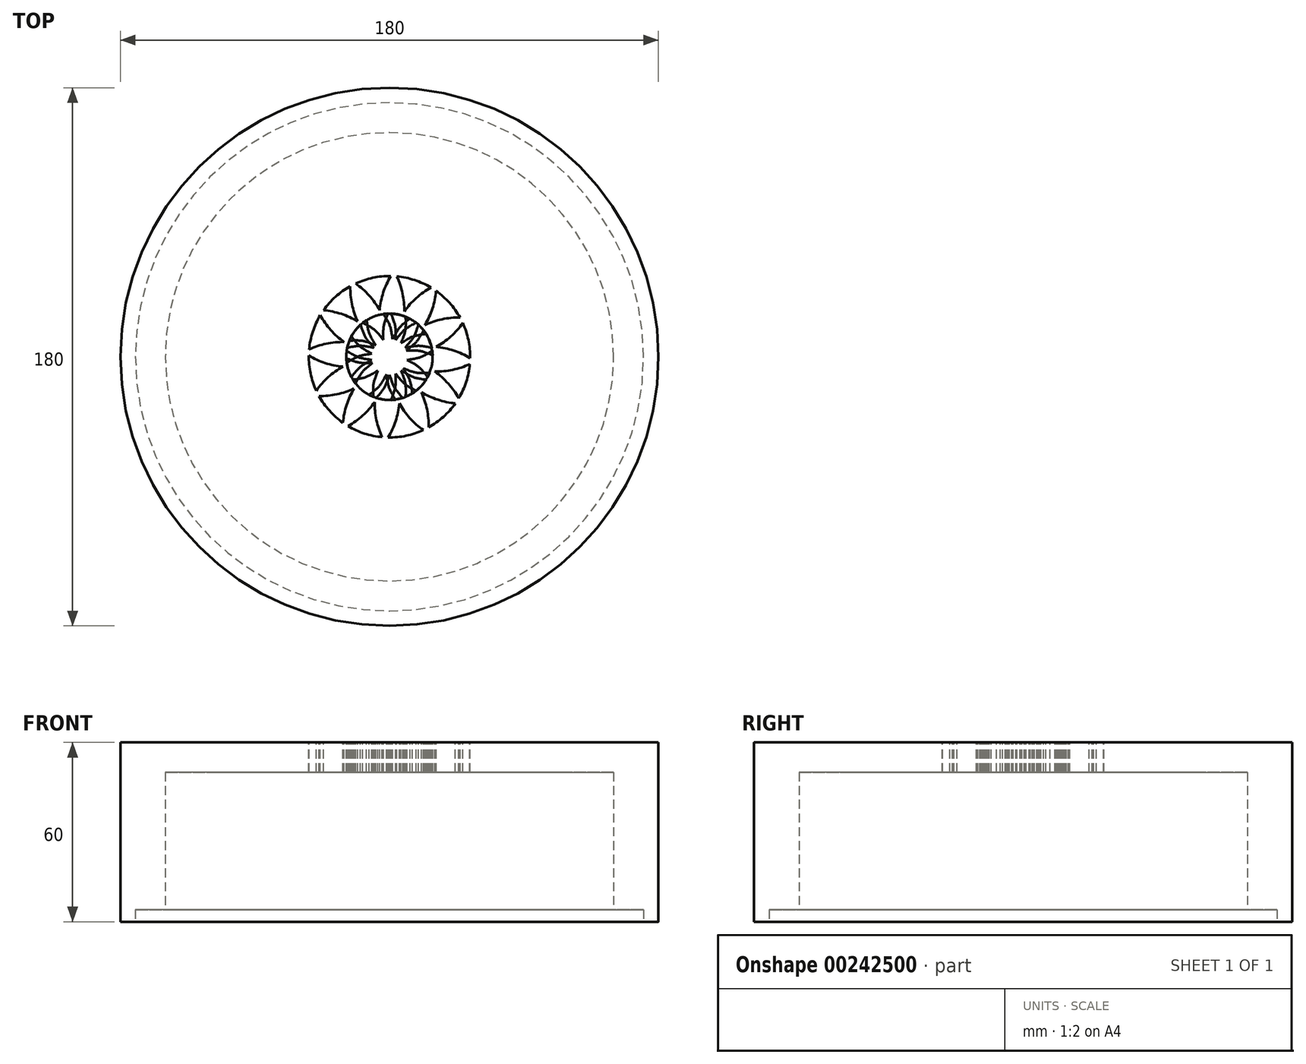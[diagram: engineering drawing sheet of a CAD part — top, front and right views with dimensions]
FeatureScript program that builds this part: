
annotation { "Feature Type Name" : "Feature", "Feature Type Description" : "" }
export const myFeature = defineFeature(function(context is Context, id is Id, definition is map)
    precondition{}
    {
        {
            var Q0;
            Q0=qCreatedBy(makeId("Top.planeOp"),FACE);
            var sketch = newSketch(context, id + "F0", { "sketchPlane" : qUnion([Q0])});
            skLineSegment(sketch, "E0", {"start": v(0, 117.16) * mm, "end": v(0, -101.17) * mm, "construction": true});
            skLineSegment(sketch, "E1", {"start": v(-126.7, 0) * mm, "end": v(131.73, 0) * mm, "construction": true});
            skLineSegment(sketch, "E2", {"start": v(0, -6) * mm, "end": v(-4.5, -13.8) * mm, "construction": true});
            skLineSegment(sketch, "E3", {"start": v(-4.5, -13.8) * mm, "end": v(4.5, -13.8) * mm, "construction": true});
            skLineSegment(sketch, "E4", {"start": v(4.5, -13.8) * mm, "end": v(0, -6) * mm, "construction": true});
            skLineSegment(sketch, "E5", {"start": v(0, -6) * mm, "end": v(0, -13.8) * mm, "construction": true});
            skFitSpline(sketch, "E6", {"points": [v(-4.5, -13.8) * mm, v(4.5, -13.8) * mm], "startDerivative": vector(13.5, -2.7) * mm, "endDerivative": vector(13.5, 2.7) * mm});
            skFitSpline(sketch, "E7", {"points": [v(-4.5, -13.8) * mm, v(0, -6) * mm], "startDerivative": vector(9.09, 10.34) * mm, "endDerivative": vector(4.41, 13.04) * mm});
            skLineSegment(sketch, "E8", {"start": v(4.5, -13.8) * mm, "end": v(-1.47, -10.35) * mm, "construction": true});
            skLineSegment(sketch, "E9", {"start": v(-4.5, -13.8) * mm, "end": v(1.47, -10.35) * mm, "construction": true});
            skFitSpline(sketch, "E10", {"points": [v(0, -6) * mm, v(4.5, -13.8) * mm], "startDerivative": vector(4.41, -13.04) * mm, "endDerivative": vector(9.09, -10.34) * mm});
            skSolve(sketch);
        }
        {
            var Q0;
            Q0=qCreatedBy(makeId("Top.planeOp"),FACE);
            var sketch = newSketch(context, id + "F1", { "sketchPlane" : qUnion([Q0])});
            skCircle(sketch, "E11", {"center": v(0, 0) * mm, "radius": 90 * mm});
            skSolve(sketch);
        }
        {
            var Q0;
            Q0 = qSketchRegion(id + "F1", true);
            extrude(context, id + "F2", {"entities" : qUnion([Q0]), "oppositeDirection" : true, "depth" : 60 * mm});
        }
        {
            var Q0;
            Q0=makeQuery(id+"F2.opExtrude","CAP_FACE",FACE,{"disambiguationData":[OSD([sQuery(id+"F1.wireOp",EDGE,"E11")])],"isStart":false});
            var sketch = newSketch(context, id + "F3", { "sketchPlane" : qUnion([Q0])});
            skCircle(sketch, "E12", {"center": v(0, 0) * mm, "radius": 85 * mm});
            skCircle(sketch, "E13", {"center": v(0, 0) * mm, "radius": 75 * mm});
            skSolve(sketch);
        }
        {
            var Q0;
            Q0 = qSketchRegion(id + "F3", true);
            extrude(context, id + "F4", {"entities" : qUnion([Q0]), "operationType" : NewBodyOperationType.REMOVE, "oppositeDirection" : true, "depth" : 4 * mm});
        }
        {
            var Q0;
            Q0=makeQuery(id+"F4.boolean.opBoolean","SPLIT",FACE,{"disambiguationData":[TD([makeQuery(id+"F4.opExtrude","SWEPT_FACE",FACE,{"disambiguationData":[OSD([sQuery(id+"F3.wireOp",EDGE,"E13")])]})])],"derivedFrom":makeQuery(id+"F2.opExtrude","CAP_FACE",FACE,{"disambiguationData":[OSD([sQuery(id+"F1.wireOp",EDGE,"E11")])],"isStart":false})});
            var sketch = newSketch(context, id + "F5", { "sketchPlane" : qUnion([Q0])});
            skSolve(sketch);
        }
        {
            var Q0;
            Q0=makeQuery(id+"F5.imprint","IMPRINT",FACE,{"disambiguationData":[TD([[makeQuery(id+"F5.imprint","IMPRINT",EDGE,{"derivedFrom":makeQuery(id+"F4.boolean.opBoolean","COPY",EDGE,{"derivedFrom":makeQuery(id+"F4.opExtrude","CAP_EDGE",EDGE,{"disambiguationData":[OSD([sQuery(id+"F3.wireOp",EDGE,"E13")])],"isStart":true})})}),1.0]])]});
            var sketch = newSketch(context, id + "F6", { "sketchPlane" : qUnion([Q0])});
            skCircle(sketch, "E14", {"center": v(0, 0) * mm, "radius": 75 * mm});
            skSolve(sketch);
        }
        {
            var Q0;
            Q0=makeQuery(id+"F5.imprint","IMPRINT",FACE,{"disambiguationData":[TD([[makeQuery(id+"F5.imprint","IMPRINT",EDGE,{"derivedFrom":makeQuery(id+"F4.boolean.opBoolean","COPY",EDGE,{"derivedFrom":makeQuery(id+"F4.opExtrude","CAP_EDGE",EDGE,{"disambiguationData":[OSD([sQuery(id+"F3.wireOp",EDGE,"E13")])],"isStart":true})})}),1.0]])]});
            extrude(context, id + "F7", {"entities" : qUnion([Q0]), "operationType" : NewBodyOperationType.REMOVE, "oppositeDirection" : true, "depth" : 50 * mm});
        }
        {
            var Q0;
            Q0 = qSketchRegion(id + "F0", true);
            extrude(context, id + "F8", {"entities" : qUnion([Q0]), "operationType" : NewBodyOperationType.REMOVE, "endBound" : BoundingType.UP_TO_NEXT, "oppositeDirection" : true, "depth" : 25 * mm});
        }
        {
            var Q0;
            Q0=makeQuery(id+"F2.opExtrude","SWEPT_BODY",BODY,{"disambiguationData":[OSD([sQuery(id+"F1.wireOp",EDGE,"E11")])]});
            var Q1;
            Q1=sQuery(id+"F6.wireOp",EDGE,"E14");
            circularPattern(context, id + "F9", {"entities" : qUnion([Q0]), "axis" : qUnion([Q1]), "angle" : 360 * degree, "instanceCount" : 9, "equalSpace" : true});
        }
        {
            var Q0;
            Q0=makeQuery(id+"F2.opExtrude","CAP_FACE",FACE,{"disambiguationData":[OSD([sQuery(id+"F1.wireOp",EDGE,"E11")])],"isStart":true});
            var sketch = newSketch(context, id + "F10", { "sketchPlane" : qUnion([Q0])});
            skFitSpline(sketch, "E15.0.0", {"points": [v(4.5, -13.8) * mm, v(1.47, -10.35) * mm, v(1.47, -10.35) * mm, v(0, -6) * mm]});
            skLineSegment(sketch, "E16", {"start": v(0, 0) * mm, "end": v(-8.16, -25.03) * mm, "construction": true});
            skCircle(sketch, "E17", {"center": v(0, 0) * mm, "radius": 27 * mm, "construction": true});
            skLineSegment(sketch, "E18", {"start": v(-4.94, -15.15) * mm, "end": v(-13.87, -23.17) * mm, "construction": true});
            skLineSegment(sketch, "E19", {"start": v(-13.87, -23.17) * mm, "end": v(-2.46, -26.89) * mm, "construction": true});
            skLineSegment(sketch, "E20", {"start": v(-2.46, -26.89) * mm, "end": v(-4.94, -15.15) * mm, "construction": true});
            skLineSegment(sketch, "E21", {"start": v(-8.16, -25.03) * mm, "end": v(-8.37, -25.67) * mm, "construction": true});
            skArc(sketch, "E22", {"start": v(-13.87, -23.17) * mm, "mid": v(-8.37, -25.67) * mm, "end": v(-2.46, -26.89) * mm});
            skLineSegment(sketch, "E23", {"start": v(-8.37, -25.67) * mm, "end": v(-9.4, -19.16) * mm, "construction": true});
            skArc(sketch, "E24", {"start": v(-13.87, -23.17) * mm, "mid": v(-8.95, -19.66) * mm, "end": v(-4.94, -15.15) * mm});
            skArc(sketch, "E25", {"start": v(-4.94, -15.15) * mm, "mid": v(-4.36, -21.16) * mm, "end": v(-2.46, -26.89) * mm});
            skArc(sketch, "E26.1.0", {"start": v(27, -0.43) * mm, "mid": v(21.5, 2.08) * mm, "end": v(15.59, 3.3) * mm});
            skArc(sketch, "E26.1.1", {"start": v(15.59, 3.3) * mm, "mid": v(20.5, 6.8) * mm, "end": v(24.52, 11.31) * mm});
            skArc(sketch, "E26.2.0", {"start": v(-13.13, 23.6) * mm, "mid": v(-12.55, 17.58) * mm, "end": v(-10.65, 11.85) * mm});
            skArc(sketch, "E26.2.1", {"start": v(-10.65, 11.85) * mm, "mid": v(-16.14, 14.36) * mm, "end": v(-22.06, 15.57) * mm});
            skSolve(sketch);
        }
        {
            var Q0;
            Q0=makeQuery(id+"F10.imprint","IMPRINT",FACE,{"disambiguationData":[TD([[makeQuery(id+"F10.imprint","IMPRINT",EDGE,{"derivedFrom":sQuery(id+"F10.wireOp",EDGE,"E22")}),1.0]])]});
            extrude(context, id + "F11", {"entities" : qUnion([Q0]), "operationType" : NewBodyOperationType.REMOVE, "endBound" : BoundingType.UP_TO_NEXT, "oppositeDirection" : true, "depth" : 25 * mm});
        }
        {
            var Q0;
            Q0=makeQuery(id+"F9.opPattern","COPY",BODY,{"derivedFrom":makeQuery(id+"F2.opExtrude","SWEPT_BODY",BODY,{"disambiguationData":[OSD([sQuery(id+"F1.wireOp",EDGE,"E11")])]}),"instanceName":"4"});
            var Q1;
            Q1=sQuery(id+"F10.wireOp",EDGE,"E17");
            circularPattern(context, id + "F12", {"entities" : qUnion([Q0]), "axis" : qUnion([Q1]), "angle" : 360 * degree, "instanceCount" : 12, "equalSpace" : true});
        }
    });
